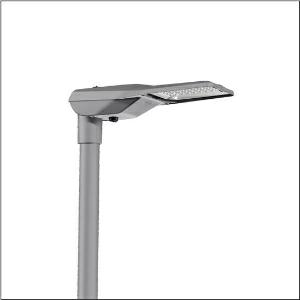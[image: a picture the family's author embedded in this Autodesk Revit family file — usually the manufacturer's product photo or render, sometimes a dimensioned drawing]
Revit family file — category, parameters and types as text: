
# Revit family: streetlight_sl_21_iq_mini___st1_0ab_5xe2m31y08hb_576a
name_source: partatom
category: Lighting Fixtures
units: mm (PartAtom-declared; Revit-internal decimal feet)

## family parameters
Cut with Voids When Loaded = No
Host = Face
Light Source = No
Part Type = Normal
Room Calculation Point = No
Round Connector Dimension = Use Diameter
Shared = No

## types (1)
- --- (1 x LED, 8580 lm, 71 W, 3000K)
    Apparent Load = 71 VA
    CIE Flux Codes = 38 73 97 100 100
    Color Rendering = 70
    Color Temperature = 3000K
    Default Elevation = 1800 mm
    Description = Streetlight SL 21 iQ mini, mast luminaire, primary light control with lens, of PMMA, primary optical cover: cover, of toughened safety glass, transparent, light distribution: ST1.0aB, light emission: direct distribution, primary light characteristic: asymmetric, installation type: post-top, side-entry, LED, High Power LED, rated luminous flux: 8.580lm, luminous efficacy: 121lm/W, light colour: 730, colour temperature: 3000K, control: presetting dimming logarithmic, Street-Remote, Auto-Match, Temp-Guard, Lumen-Switch, Night-Set, Smart-Wire, Light-Fading, Desk-Remote (wireless, voltage-free reading and setting of iQ features in the workshop via application-optimized NFC function/RFID function), optimised constant luminous flux control (CLO 2.0), mains connection: 220..240V, AC, 50/60Hz, start of lifetime: 71W, end of service life: 75W, reduction: 30W, luminaire housing, of diecast aluminium, powder-coated, Siteco® metallic grey (DB 702S), corrosivity category C5 mid according to DIN EN ISO 12944, please order mast flange separately, inclination adjustable: 0°, 5°, 10°, 15°, sealing non-destructively replaceable, multi-level sealing system, length: 628mm, width: 235mm, height: 110mm, mast flange for spigot size: 42mm (side-entry): 5XC10008XM4, 60/48mm (side-entry/post-top): 5XC10108XM2, 76/60mm (side-entry/post-top): 5XC10108XM1, Smart Interface below and above, protection rating (complete): IP66, insulation class (complete): insulation class II (safety insulation), certification: CE, ENEC, ENEC+, VDE, impact resistance: IK09, permissible operating ambient temperature for outdoor applications: -40..+50°C, standard-compliant lighting for roads and squares, packaging unit: 1 piece

Light Distribution: ST1.0aB
    Height = 110 mm
    Lamp = 1 x LED
    Lamp Light Flux = 8580 lm
    Lamp Power = 71 W
    Lamp count = 1
    Length = 625 mm
    Luminous efficacy = 121 lm/W
    Manufacturer = Siteco
    ModVariant = No
    Model = 5XE2M31Y08HB
    Number of Poles = 1
    OnlyDefault = Yes
    Power Factor = 1
    Product Name = Streetlight SL 21 iQ mini | ST1.0aB
    Product group = mast luminaire | pylon top
    ProductGroupID = 6100
    Protection Class = Protection class II
    Protection Degree = IP 66
    RLX_Detail_Level = 1
    RLX_Emergency_Light_Flux = 0 lm
    RLX_Emergency_Type = 0
    RLX_Emergency_Type_DB = No
    RlxData = <blob elided: 92537 chars, md5=f1bc1133>
    Socket = socket
    Standby Power = 0 W
    System Light Flux = 8580 lm
    System Power = 71 W
    Type Comments = factory setting: luminous flux: 100 % | dim-lin: 254 | 716 mA
    Type Image = l_1003514.jpg
    URL = http://relux.com
    VarID = @adj_042483
    Voltage = 0 V
    Weight = 0.00 kg
    Width = 234 mm

## geometry (parser evidence)
native form markers: Blend x4, Sweep x10
no freeform markers — native parametric forms only
